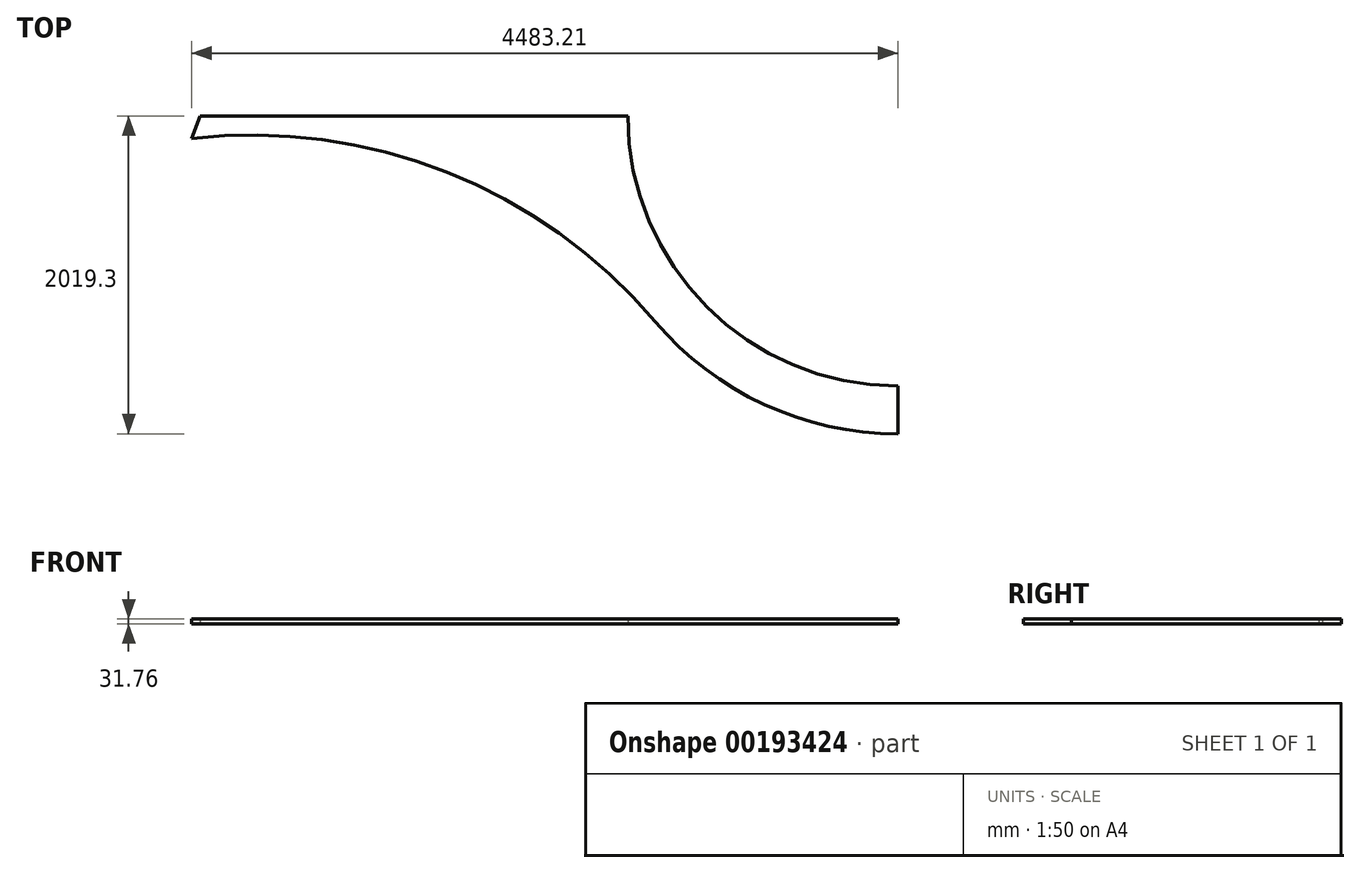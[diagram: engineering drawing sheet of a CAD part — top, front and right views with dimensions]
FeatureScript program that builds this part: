
annotation { "Feature Type Name" : "Feature", "Feature Type Description" : "" }
export const myFeature = defineFeature(function(context is Context, id is Id, definition is map)
    precondition{}
    {
        {
            var Q0;
            Q0=qCreatedBy(makeId("Top.planeOp"),FACE);
            var sketch = newSketch(context, id + "F0", { "sketchPlane" : qUnion([Q0])});
            skLineSegment(sketch, "E0", {"start": v(-2212.93, 30.25) * mm, "end": v(504.87, 30.25) * mm});
            skLineSegment(sketch, "E1", {"start": v(2219.37, -1684.25) * mm, "end": v(2219.37, -2293.85) * mm});
            skArc(sketch, "E2", {"start": v(2219.37, -1684.25) * mm, "mid": v(1007.03, -1182.09) * mm, "end": v(504.87, 30.25) * mm});
            skArc(sketch, "E3.0", {"start": v(2219.37, -1989.05) * mm, "mid": v(1370.33, -1801.89) * mm, "end": v(678.68, -1275.08) * mm});
            skArc(sketch, "E4.0", {"start": v(2219.37, -2293.85) * mm, "mid": v(1242.17, -2078.43) * mm, "end": v(446.13, -1472.1) * mm});
            skLineSegment(sketch, "E5", {"start": v(-2212.93, 30.25) * mm, "end": v(-2378.66, -437.43) * mm});
            skPoint(sketch, "E6", {"position": v(-2263.84, -113.4) * mm});
            skArc(sketch, "E7", {"start": v(678.68, -1275.08) * mm, "mid": v(-646.77, -324.9) * mm, "end": v(-2263.84, -113.4) * mm});
            skArc(sketch, "E8.0", {"start": v(446.13, -1472.1) * mm, "mid": v(-829.53, -581.46) * mm, "end": v(-2378.66, -437.43) * mm});
            skPoint(sketch, "E9.orphan", {"position": v(-2675.5, -1275.08) * mm});
            skSolve(sketch);
        }
        {
            var Q0;
            {var subQ4=sQuery(id+"F0.wireOp",EDGE,"E0");Q0=makeQuery(id+"F0.imprint","IMPRINT",FACE,{"disambiguationData":[TD([[makeQuery(id+"F0.imprint","IMPRINT",EDGE,{"derivedFrom":subQ4}),-1.0]])]});}
            var Q1;
            {var subQ4=sQuery(id+"F0.wireOp",EDGE,"E3.0");Q1=makeQuery(id+"F0.imprint","IMPRINT",FACE,{"disambiguationData":[TD([[makeQuery(id+"F0.imprint","IMPRINT",EDGE,{"derivedFrom":subQ4}),1.0]])]});}
            extrude(context, id + "F1", {"entities" : qUnion([Q0, Q1]), "endBound" : BoundingType.SYMMETRIC, "depth" : 31.75 * mm});
        }
    });
